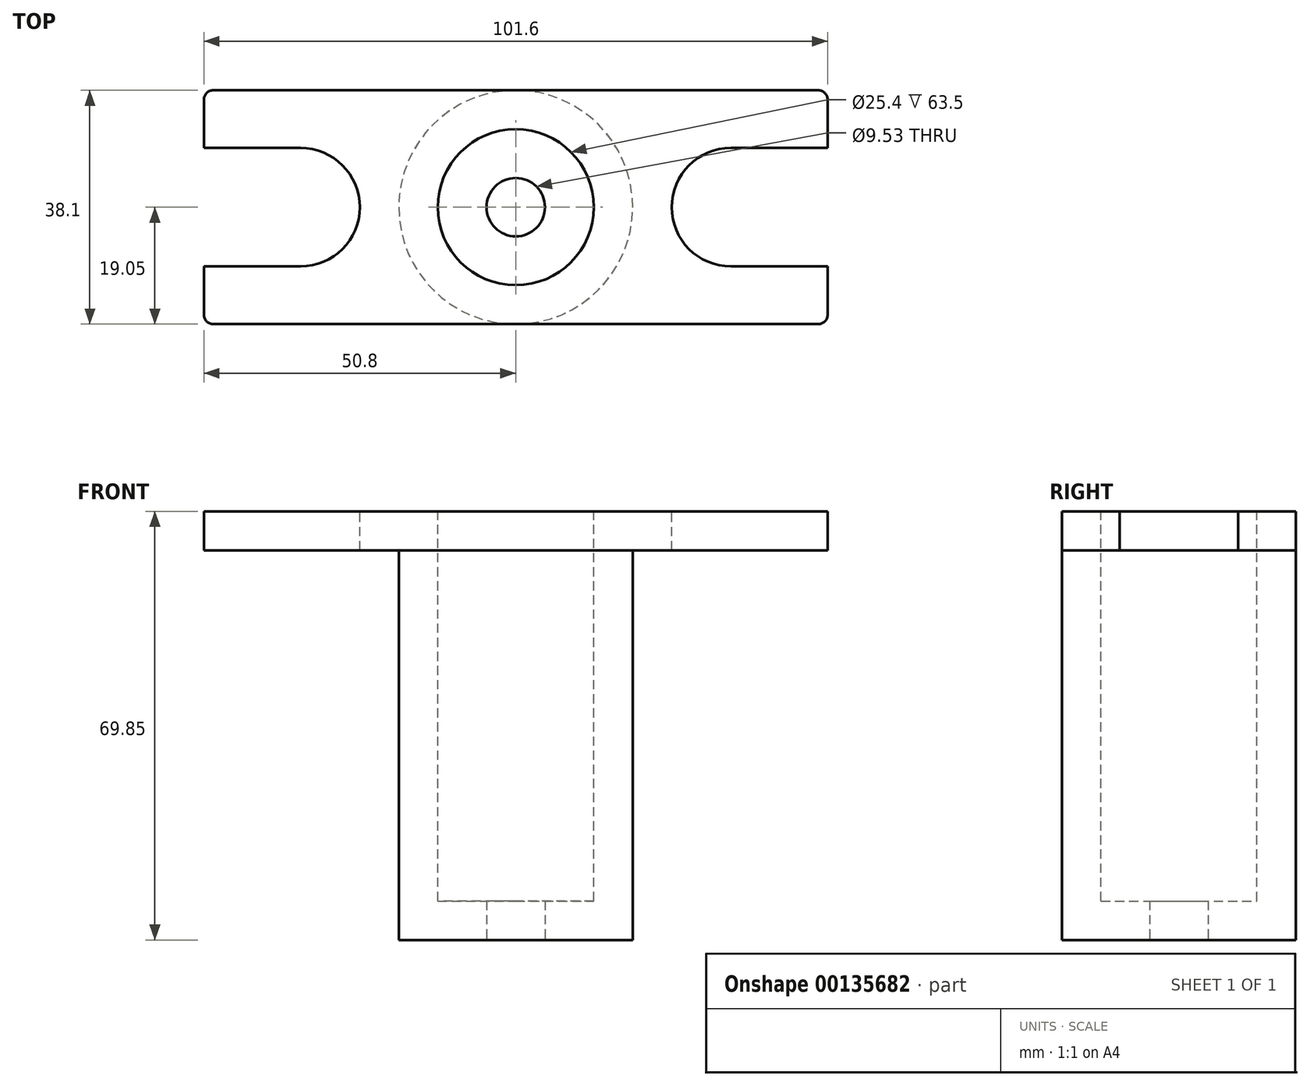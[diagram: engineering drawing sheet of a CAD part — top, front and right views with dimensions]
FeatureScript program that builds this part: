
annotation { "Feature Type Name" : "Feature", "Feature Type Description" : "" }
export const myFeature = defineFeature(function(context is Context, id is Id, definition is map)
    precondition{}
    {
        {
            var Q0;
            Q0=qCreatedBy(makeId("Top.planeOp"),FACE);
            var sketch = newSketch(context, id + "F0", { "sketchPlane" : qUnion([Q0])});
            skCircle(sketch, "E0", {"center": v(0, 0) * mm, "radius": 19.05 * mm});
            skSolve(sketch);
        }
        {
            var Q0;
            Q0=qSketchRegion(id+"F0",true);
            extrude(context, id + "F1", {"entities" : qUnion([Q0]), "depth" : 69.85 * mm});
        }
        {
            var Q0;
            Q0=makeQuery(id+"F1.opExtrude","CAP_FACE",FACE,{"disambiguationData":[OSD([sQuery(id+"F0.wireOp",EDGE,"E0")])],"isStart":false});
            var sketch = newSketch(context, id + "F2", { "sketchPlane" : qUnion([Q0])});
            skCircle(sketch, "E1", {"center": v(0, 0) * mm, "radius": 12.7 * mm});
            skSolve(sketch);
        }
        {
            var Q0;
            Q0=qSketchRegion(id+"F2",true);
            extrude(context, id + "F3", {"entities" : qUnion([Q0]), "operationType" : NewBodyOperationType.REMOVE, "oppositeDirection" : true, "depth" : 63.5 * mm});
        }
        {
            var Q0;
            Q0=makeQuery(id+"F1.opExtrude","CAP_FACE",FACE,{"disambiguationData":[OSD([sQuery(id+"F0.wireOp",EDGE,"E0")])],"isStart":true});
            var sketch = newSketch(context, id + "F4", { "sketchPlane" : qUnion([Q0])});
            skCircle(sketch, "E2", {"center": v(0, 0) * mm, "radius": 4.76 * mm});
            skSolve(sketch);
        }
        {
            var Q0;
            Q0=qSketchRegion(id+"F4",true);
            extrude(context, id + "F5", {"entities" : qUnion([Q0]), "operationType" : NewBodyOperationType.REMOVE, "endBound" : BoundingType.THROUGH_ALL, "oppositeDirection" : true, "depth" : 25.4 * mm});
        }
        {
            var Q0;
            Q0=makeQuery(id+"F1.opExtrude","CAP_FACE",FACE,{"disambiguationData":[OSD([sQuery(id+"F0.wireOp",EDGE,"E0")])],"isStart":false});
            var sketch = newSketch(context, id + "F6", { "sketchPlane" : qUnion([Q0])});
            skLineSegment(sketch, "E3.bottom", {"start": v(17.53, -50.8) * mm, "end": v(-17.53, -50.8) * mm});
            skLineSegment(sketch, "E3.top", {"start": v(17.53, 50.8) * mm, "end": v(-17.53, 50.8) * mm});
            skLineSegment(sketch, "E3.left", {"start": v(19.05, -49.28) * mm, "end": v(19.05, 49.28) * mm});
            skLineSegment(sketch, "E3.right", {"start": v(-19.05, -49.28) * mm, "end": v(-19.05, 49.28) * mm});
            skPoint(sketch, "E4.visualSharp", {"position": v(19.05, -50.8) * mm});
            skArc(sketch, "E4.filletArc", {"start": v(17.53, -50.8) * mm, "mid": v(18.6, -50.35) * mm, "end": v(19.05, -49.28) * mm});
            skPoint(sketch, "E5.visualSharp", {"position": v(-19.05, -50.8) * mm});
            skArc(sketch, "E5.filletArc", {"start": v(-19.05, -49.28) * mm, "mid": v(-18.6, -50.35) * mm, "end": v(-17.53, -50.8) * mm});
            skPoint(sketch, "E6.visualSharp", {"position": v(19.05, 50.8) * mm});
            skArc(sketch, "E6.filletArc", {"start": v(19.05, 49.28) * mm, "mid": v(18.6, 50.35) * mm, "end": v(17.53, 50.8) * mm});
            skPoint(sketch, "E7.visualSharp", {"position": v(-19.05, 50.8) * mm});
            skArc(sketch, "E7.filletArc", {"start": v(-17.53, 50.8) * mm, "mid": v(-18.6, 50.35) * mm, "end": v(-19.05, 49.28) * mm});
            skArc(sketch, "E8", {"start": v(-9.65, 35.05) * mm, "mid": v(0, 25.4) * mm, "end": v(9.65, 35.05) * mm});
            skLineSegment(sketch, "E9", {"start": v(24.8, 0) * mm, "end": v(-28.36, 0) * mm, "construction": true});
            skLineSegment(sketch, "E10", {"start": v(9.65, 35.05) * mm, "end": v(9.65, 50.8) * mm});
            skLineSegment(sketch, "E11", {"start": v(-9.65, 35.05) * mm, "end": v(-9.65, 50.8) * mm});
            skLineSegment(sketch, "E12", {"start": v(9.65, 50.8) * mm, "end": v(-9.65, 50.8) * mm});
            skArc(sketch, "E13.MirrorCS", {"start": v(-9.65, -35.05) * mm, "mid": v(0, -25.4) * mm, "end": v(9.65, -35.05) * mm});
            skLineSegment(sketch, "E14.MirrorCS", {"start": v(9.65, -35.05) * mm, "end": v(9.65, -50.8) * mm});
            skLineSegment(sketch, "E15.MirrorCS", {"start": v(-9.65, -35.05) * mm, "end": v(-9.65, -50.8) * mm});
            skLineSegment(sketch, "E16", {"start": v(9.65, -50.8) * mm, "end": v(-9.65, -50.8) * mm});
            skSolve(sketch);
        }
        {
            var Q0;
            {var subQ9=sQuery(id+"F6.wireOp",EDGE,"E4.filletArc");Q0=makeQuery(id+"F6.imprint","IMPRINT",FACE,{"disambiguationData":[TD([[makeQuery(id+"F6.imprint","IMPRINT",EDGE,{"derivedFrom":subQ9}),1.0]])]});}
            var Q1;
            {var subQ0=sQuery(id+"F6.wireOp",EDGE,"E6.filletArc");Q1=makeQuery(id+"F6.imprint","IMPRINT",FACE,{"disambiguationData":[TD([[makeQuery(id+"F6.imprint","IMPRINT",EDGE,{"derivedFrom":subQ0}),1.0]])]});}
            extrude(context, id + "F7", {"entities" : qUnion([Q0, Q1]), "operationType" : NewBodyOperationType.ADD, "oppositeDirection" : true, "depth" : 6.35 * mm});
        }
        {
            var Q0;
            Q0=makeQuery(id+"F1.opExtrude","SWEPT_BODY",BODY,{"disambiguationData":[OSD([sQuery(id+"F0.wireOp",EDGE,"E0")])]});
            var Q1;
            Q1=makeQuery(id+"F3.boolean.opBoolean","COPY",FACE,{"derivedFrom":makeQuery(id+"F3.opExtrude","SWEPT_FACE",FACE,{"disambiguationData":[OSD([sQuery(id+"F2.wireOp",EDGE,"E1")])]})});
            transform(context, id + "F8", {"entities" : qUnion([Q0]), "transformType" : TransformType.ROTATION, "transformAxis" : qUnion([Q1]), "angle" : 90 * degree, "makeCopy" : false});
        }
    });
